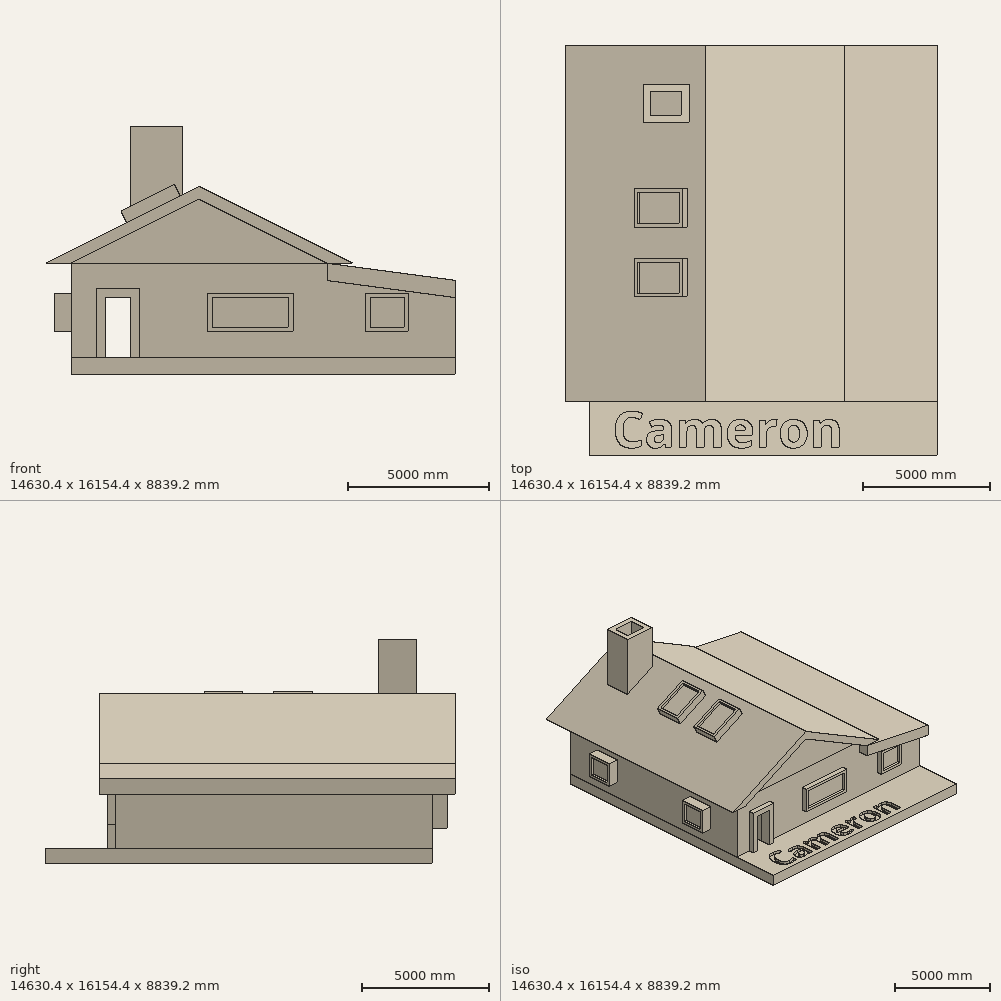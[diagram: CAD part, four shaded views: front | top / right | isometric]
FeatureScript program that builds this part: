
annotation { "Feature Type Name" : "Feature", "Feature Type Description" : "" }
export const myFeature = defineFeature(function(context is Context, id is Id, definition is map)
    precondition{}
    {
        {
            var Q0;
            Q0=qCreatedBy(makeId("Front.planeOp"),FACE);
            var sketch = newSketch(context, id + "F0", { "sketchPlane" : qUnion([Q0])});
            skLineSegment(sketch, "E0", {"start": v(0, 0) * mm, "end": v(-4572, 0) * mm});
            skLineSegment(sketch, "E1", {"start": v(0, 0) * mm, "end": v(4572, 0) * mm});
            skLineSegment(sketch, "E2", {"start": v(0, 0) * mm, "end": v(0, 2286) * mm});
            skLineSegment(sketch, "E3", {"start": v(-4572, 0) * mm, "end": v(0, 2286) * mm});
            skLineSegment(sketch, "E4", {"start": v(0, 2286) * mm, "end": v(4572, 0) * mm});
            skLineSegment(sketch, "E5.bottom", {"start": v(-4572, 0) * mm, "end": v(4572, 0) * mm});
            skLineSegment(sketch, "E5.top", {"start": v(-4572, -3352.8) * mm, "end": v(4572, -3352.8) * mm});
            skLineSegment(sketch, "E5.left", {"start": v(-4572, 0) * mm, "end": v(-4572, -3352.8) * mm});
            skLineSegment(sketch, "E5.right", {"start": v(4572, 0) * mm, "end": v(4572, -3352.8) * mm});
            skLineSegment(sketch, "E6", {"start": v(-4572, 0) * mm, "end": v(-5486.4, 0) * mm});
            skLineSegment(sketch, "E7", {"start": v(4572, 0) * mm, "end": v(5486.4, 0) * mm});
            skLineSegment(sketch, "E8", {"start": v(0, 2286) * mm, "end": v(0, 2743.2) * mm});
            skLineSegment(sketch, "E9", {"start": v(0, 2743.2) * mm, "end": v(-5486.4, 0) * mm});
            skLineSegment(sketch, "E10", {"start": v(0, 2743.2) * mm, "end": v(5486.4, 0) * mm});
            skLineSegment(sketch, "E11", {"start": v(4572, -3352.8) * mm, "end": v(9144, -3352.8) * mm});
            skLineSegment(sketch, "E12", {"start": v(9144, -3352.8) * mm, "end": v(9144, -609.6) * mm});
            skLineSegment(sketch, "E13", {"start": v(9144, -609.6) * mm, "end": v(4572, 0) * mm});
            skLineSegment(sketch, "E14.0", {"start": v(9144, -1224.6) * mm, "end": v(4572, -615) * mm});
            skLineSegment(sketch, "E15.0", {"start": v(4572, -3962.4) * mm, "end": v(9144, -3962.4) * mm});
            skLineSegment(sketch, "E15.1", {"start": v(-4572, -3962.4) * mm, "end": v(4572, -3962.4) * mm});
            skLineSegment(sketch, "E16", {"start": v(-4572, -3962.4) * mm, "end": v(-4572, -3352.8) * mm});
            skLineSegment(sketch, "E17", {"start": v(4572, -3962.4) * mm, "end": v(4572, -3352.8) * mm});
            skLineSegment(sketch, "E18", {"start": v(9144, -3962.4) * mm, "end": v(9144, -3352.8) * mm});
            skLineSegment(sketch, "E19", {"start": v(-3352.8, -3352.8) * mm, "end": v(-2438.4, -3352.8) * mm});
            skLineSegment(sketch, "E20", {"start": v(-2438.4, -3352.8) * mm, "end": v(-2438.4, -1219.2) * mm});
            skLineSegment(sketch, "E21", {"start": v(-2438.4, -1219.2) * mm, "end": v(-3352.8, -1219.2) * mm});
            skLineSegment(sketch, "E22", {"start": v(-3352.8, -1219.2) * mm, "end": v(-3352.8, -3352.8) * mm});
            skLineSegment(sketch, "E23.0", {"start": v(-3657.6, -914.4) * mm, "end": v(-3657.6, -3352.8) * mm});
            skLineSegment(sketch, "E23.1", {"start": v(-2133.6, -914.4) * mm, "end": v(-3657.6, -914.4) * mm});
            skLineSegment(sketch, "E23.2", {"start": v(-2133.6, -3352.8) * mm, "end": v(-2133.6, -914.4) * mm});
            skLineSegment(sketch, "E24", {"start": v(-3657.6, -3352.8) * mm, "end": v(-3352.8, -3352.8) * mm});
            skLineSegment(sketch, "E25", {"start": v(-2438.4, -3352.8) * mm, "end": v(-2133.6, -3352.8) * mm});
            skLineSegment(sketch, "E26", {"start": v(457.2, -2286) * mm, "end": v(3200.4, -2286) * mm});
            skLineSegment(sketch, "E27", {"start": v(457.2, -2286) * mm, "end": v(457.2, -1219.2) * mm});
            skLineSegment(sketch, "E28", {"start": v(457.2, -1219.2) * mm, "end": v(3200.4, -1219.2) * mm});
            skLineSegment(sketch, "E29", {"start": v(3200.4, -1219.2) * mm, "end": v(3200.4, -2286) * mm});
            skLineSegment(sketch, "E30.0", {"start": v(304.8, -2438.4) * mm, "end": v(304.8, -1066.8) * mm});
            skLineSegment(sketch, "E30.1", {"start": v(304.8, -2438.4) * mm, "end": v(3352.8, -2438.4) * mm});
            skLineSegment(sketch, "E30.2", {"start": v(3352.8, -1066.8) * mm, "end": v(3352.8, -2438.4) * mm});
            skLineSegment(sketch, "E30.3", {"start": v(304.8, -1066.8) * mm, "end": v(3352.8, -1066.8) * mm});
            skLineSegment(sketch, "E31", {"start": v(6096, -2286) * mm, "end": v(6096, -1219.2) * mm});
            skLineSegment(sketch, "E32", {"start": v(6096, -2286) * mm, "end": v(7315.2, -2286) * mm});
            skLineSegment(sketch, "E33", {"start": v(7315.2, -2286) * mm, "end": v(7315.2, -1219.2) * mm});
            skLineSegment(sketch, "E34", {"start": v(7315.2, -1219.2) * mm, "end": v(6096, -1219.2) * mm});
            skLineSegment(sketch, "E35.0", {"start": v(7467.6, -1066.8) * mm, "end": v(5943.6, -1066.8) * mm});
            skLineSegment(sketch, "E35.1", {"start": v(7467.6, -2438.4) * mm, "end": v(7467.6, -1066.8) * mm});
            skLineSegment(sketch, "E35.2", {"start": v(5943.6, -2438.4) * mm, "end": v(7467.6, -2438.4) * mm});
            skLineSegment(sketch, "E35.3", {"start": v(5943.6, -2438.4) * mm, "end": v(5943.6, -1066.8) * mm});
            skSolve(sketch);
        }
        {
            var Q0;
            Q0=makeQuery(id+"F0.imprint","IMPRINT",FACE,{"disambiguationData":[TD([[makeQuery(id+"F0.imprint","IMPRINT",EDGE,{"derivedFrom":sQuery(id+"F0.wireOp",EDGE,"E3")}),1.0]])]});
            var Q1;
            Q1=makeQuery(id+"F0.imprint","IMPRINT",FACE,{"disambiguationData":[TD([[makeQuery(id+"F0.imprint","IMPRINT",EDGE,{"derivedFrom":sQuery(id+"F0.wireOp",EDGE,"E4")}),1.0]])]});
            var Q2;
            {var subQ0=sQuery(id+"F0.wireOp",EDGE,"E13");Q2=makeQuery(id+"F0.imprint","IMPRINT",FACE,{"disambiguationData":[TD([[makeQuery(id+"F0.imprint","IMPRINT",EDGE,{"derivedFrom":subQ0}),1.0]])]});}
            extrude(context, id + "F1", {"entities" : qUnion([Q0, Q1, Q2]), "depth" : 914.4 * mm, "offsetDistance" : 30.48 * mm, "hasSecondDirection" : true, "secondDirectionOppositeDirection" : true, "secondDirectionDepth" : 13106.4 * mm});
        }
        {
            var Q0;
            {var subQ0=sQuery(id+"F0.wireOp",EDGE,"E2");Q0=makeQuery(id+"F0.imprint","IMPRINT",FACE,{"disambiguationData":[TD([[makeQuery(id+"F0.imprint","IMPRINT",EDGE,{"derivedFrom":subQ0}),1.0]])]});}
            var Q1;
            {var subQ0=sQuery(id+"F0.wireOp",EDGE,"E2");Q1=makeQuery(id+"F0.imprint","IMPRINT",FACE,{"disambiguationData":[TD([[makeQuery(id+"F0.imprint","IMPRINT",EDGE,{"derivedFrom":subQ0}),-1.0]])]});}
            extrude(context, id + "F2", {"entities" : qUnion([Q0, Q1]), "operationType" : NewBodyOperationType.ADD, "depth" : 304.8 * mm, "offsetDistance" : 30.48 * mm, "hasSecondDirection" : true, "secondDirectionOppositeDirection" : true, "secondDirectionDepth" : 12192 * mm});
        }
        {
            var Q0;
            Q0=makeQuery(id+"F0.imprint","IMPRINT",FACE,{"disambiguationData":[TD([[makeQuery(id+"F0.imprint","IMPRINT",EDGE,{"derivedFrom":sQuery(id+"F0.wireOp",EDGE,"E15.1")}),1.0]])]});
            var Q1;
            Q1=makeQuery(id+"F0.imprint","IMPRINT",FACE,{"disambiguationData":[TD([[makeQuery(id+"F0.imprint","IMPRINT",EDGE,{"derivedFrom":sQuery(id+"F0.wireOp",EDGE,"E11")}),-1.0]])]});
            extrude(context, id + "F3", {"entities" : qUnion([Q0, Q1]), "depth" : 3048 * mm, "offsetDistance" : 30.48 * mm, "hasSecondDirection" : true, "secondDirectionOppositeDirection" : true, "secondDirectionDepth" : 12192 * mm});
        }
        {
            var Q0;
            {var subQ7=sQuery(id+"F0.wireOp",EDGE,"E5.left");Q0=makeQuery(id+"F0.imprint","IMPRINT",FACE,{"disambiguationData":[TD([[makeQuery(id+"F0.imprint","IMPRINT",EDGE,{"derivedFrom":subQ7}),1.0]])]});}
            var Q1;
            Q1=makeQuery(id+"F0.imprint","IMPRINT",FACE,{"disambiguationData":[TD([[makeQuery(id+"F0.imprint","IMPRINT",EDGE,{"derivedFrom":sQuery(id+"F0.wireOp",EDGE,"E20")}),-1.0]])]});
            var Q2;
            Q2=makeQuery(id+"F0.imprint","IMPRINT",FACE,{"disambiguationData":[TD([[makeQuery(id+"F0.imprint","IMPRINT",EDGE,{"derivedFrom":sQuery(id+"F0.wireOp",EDGE,"E19")}),1.0]])]});
            var Q3;
            Q3=makeQuery(id+"F0.imprint","IMPRINT",FACE,{"disambiguationData":[TD([[makeQuery(id+"F0.imprint","IMPRINT",EDGE,{"derivedFrom":sQuery(id+"F0.wireOp",EDGE,"E26")}),1.0]])]});
            var Q4;
            Q4=makeQuery(id+"F0.imprint","IMPRINT",FACE,{"disambiguationData":[TD([[makeQuery(id+"F0.imprint","IMPRINT",EDGE,{"derivedFrom":sQuery(id+"F0.wireOp",EDGE,"E26")}),-1.0]])]});
            var Q5;
            Q5=makeQuery(id+"F0.imprint","IMPRINT",FACE,{"disambiguationData":[TD([[makeQuery(id+"F0.imprint","IMPRINT",EDGE,{"derivedFrom":sQuery(id+"F0.wireOp",EDGE,"E31")}),-1.0]])]});
            var Q6;
            Q6=makeQuery(id+"F0.imprint","IMPRINT",FACE,{"disambiguationData":[TD([[makeQuery(id+"F0.imprint","IMPRINT",EDGE,{"derivedFrom":sQuery(id+"F0.wireOp",EDGE,"E31")}),1.0]])]});
            var Q7;
            {var subQ1=sQuery(id+"F0.wireOp",EDGE,"E11");Q7=makeQuery(id+"F0.imprint","IMPRINT",FACE,{"disambiguationData":[TD([[makeQuery(id+"F0.imprint","IMPRINT",EDGE,{"derivedFrom":subQ1}),1.0]])]});}
            extrude(context, id + "F4", {"entities" : qUnion([Q0, Q1, Q2, Q3, Q4, Q5, Q6, Q7]), "depth" : 304.8 * mm, "offsetDistance" : 30.48 * mm, "hasSecondDirection" : true, "secondDirectionOppositeDirection" : true, "secondDirectionDepth" : 12192 * mm});
        }
        {
            var Q0;
            Q0=makeQuery(id+"F0.imprint","IMPRINT",FACE,{"disambiguationData":[TD([[makeQuery(id+"F0.imprint","IMPRINT",EDGE,{"derivedFrom":sQuery(id+"F0.wireOp",EDGE,"E19")}),1.0]])]});
            var Q1;
            Q1=makeQuery(id+"F0.imprint","IMPRINT",FACE,{"disambiguationData":[TD([[makeQuery(id+"F0.imprint","IMPRINT",EDGE,{"derivedFrom":sQuery(id+"F0.wireOp",EDGE,"E26")}),1.0]])]});
            var Q2;
            Q2=makeQuery(id+"F0.imprint","IMPRINT",FACE,{"disambiguationData":[TD([[makeQuery(id+"F0.imprint","IMPRINT",EDGE,{"derivedFrom":sQuery(id+"F0.wireOp",EDGE,"E31")}),-1.0]])]});
            extrude(context, id + "F5", {"entities" : qUnion([Q0, Q1, Q2]), "depth" : 457.2 * mm, "offsetDistance" : 30.48 * mm});
        }
        {
            var Q0;
            Q0=makeQuery(id+"F0.imprint","IMPRINT",FACE,{"disambiguationData":[TD([[makeQuery(id+"F0.imprint","IMPRINT",EDGE,{"derivedFrom":sQuery(id+"F0.wireOp",EDGE,"E20")}),-1.0]])]});
            var Q1;
            Q1=makeQuery(id+"F0.imprint","IMPRINT",FACE,{"disambiguationData":[TD([[makeQuery(id+"F0.imprint","IMPRINT",EDGE,{"derivedFrom":sQuery(id+"F0.wireOp",EDGE,"E26")}),-1.0]])]});
            var Q2;
            Q2=makeQuery(id+"F0.imprint","IMPRINT",FACE,{"disambiguationData":[TD([[makeQuery(id+"F0.imprint","IMPRINT",EDGE,{"derivedFrom":sQuery(id+"F0.wireOp",EDGE,"E31")}),1.0]])]});
            extrude(context, id + "F6", {"entities" : qUnion([Q0, Q1, Q2]), "depth" : 609.6 * mm, "offsetDistance" : 30.48 * mm});
        }
        {
            var Q0;
            Q0=makeQuery(id+"F4.opExtrude","SWEPT_FACE",FACE,{"disambiguationData":[OSD([sQuery(id+"F0.wireOp",EDGE,"E5.left")])]});
            var sketch = newSketch(context, id + "F7", { "sketchPlane" : qUnion([Q0])});
            skLineSegment(sketch, "E36", {"start": v(-10058.4, -1219.2) * mm, "end": v(-10058.4, -2286) * mm});
            skLineSegment(sketch, "E37", {"start": v(-10058.4, -1219.2) * mm, "end": v(-8839.2, -1219.2) * mm});
            skLineSegment(sketch, "E38", {"start": v(-8839.2, -1219.2) * mm, "end": v(-8839.2, -2286) * mm});
            skLineSegment(sketch, "E39", {"start": v(-8839.2, -2286) * mm, "end": v(-10058.4, -2286) * mm});
            skLineSegment(sketch, "E40", {"start": v(-3048, -1219.2) * mm, "end": v(-3048, -2286) * mm});
            skLineSegment(sketch, "E41", {"start": v(-3048, -2286) * mm, "end": v(-1828.8, -2286) * mm});
            skLineSegment(sketch, "E42", {"start": v(-1828.8, -2286) * mm, "end": v(-1828.8, -1219.2) * mm});
            skLineSegment(sketch, "E43", {"start": v(-1828.8, -1219.2) * mm, "end": v(-3048, -1219.2) * mm});
            skLineSegment(sketch, "E44.0", {"start": v(-10210.8, -1066.8) * mm, "end": v(-8686.8, -1066.8) * mm});
            skLineSegment(sketch, "E44.1", {"start": v(-10210.8, -1066.8) * mm, "end": v(-10210.8, -2438.4) * mm});
            skLineSegment(sketch, "E44.2", {"start": v(-8686.8, -2438.4) * mm, "end": v(-10210.8, -2438.4) * mm});
            skLineSegment(sketch, "E44.3", {"start": v(-8686.8, -1066.8) * mm, "end": v(-8686.8, -2438.4) * mm});
            skLineSegment(sketch, "E45.0", {"start": v(-1676.4, -1066.8) * mm, "end": v(-3200.4, -1066.8) * mm});
            skLineSegment(sketch, "E45.1", {"start": v(-1676.4, -2438.4) * mm, "end": v(-1676.4, -1066.8) * mm});
            skLineSegment(sketch, "E45.2", {"start": v(-3200.4, -2438.4) * mm, "end": v(-1676.4, -2438.4) * mm});
            skLineSegment(sketch, "E45.3", {"start": v(-3200.4, -1066.8) * mm, "end": v(-3200.4, -2438.4) * mm});
            skSolve(sketch);
        }
        {
            var Q0;
            Q0=makeQuery(id+"F7.imprint","IMPRINT",FACE,{"disambiguationData":[TD([[makeQuery(id+"F7.imprint","IMPRINT",EDGE,{"derivedFrom":sQuery(id+"F7.wireOp",EDGE,"E36")}),1.0]])]});
            extrude(context, id + "F8", {"entities" : qUnion([Q0]), "operationType" : NewBodyOperationType.ADD, "depth" : 457.2 * mm, "offsetDistance" : 30.48 * mm});
        }
        {
            var Q0;
            Q0=makeQuery(id+"F1.opExtrude","SWEPT_FACE",FACE,{"disambiguationData":[OSD([sQuery(id+"F0.wireOp",EDGE,"E9")])]});
            var sketch = newSketch(context, id + "F9", { "sketchPlane" : qUnion([Q0])});
            skLineSegment(sketch, "E46", {"start": v(312.4, 6096) * mm, "end": v(312.4, 7315.2) * mm});
            skLineSegment(sketch, "E47", {"start": v(312.4, 7315.2) * mm, "end": v(-1516.4, 7315.2) * mm});
            skLineSegment(sketch, "E48", {"start": v(-1516.4, 6096) * mm, "end": v(312.4, 6096) * mm});
            skLineSegment(sketch, "E49", {"start": v(312.4, 4572) * mm, "end": v(312.4, 3352.8) * mm});
            skLineSegment(sketch, "E50", {"start": v(312.4, 3352.8) * mm, "end": v(-1516.4, 3352.8) * mm});
            skLineSegment(sketch, "E51", {"start": v(-1516.4, 3352.8) * mm, "end": v(-1516.4, 4572) * mm});
            skLineSegment(sketch, "E52", {"start": v(-1516.4, 4572) * mm, "end": v(312.4, 4572) * mm});
            skLineSegment(sketch, "E53", {"start": v(-1516.4, 6096) * mm, "end": v(-1516.4, 7315.2) * mm});
            skLineSegment(sketch, "E54.0", {"start": v(-1668.8, 3200.4) * mm, "end": v(-1668.8, 4724.4) * mm});
            skLineSegment(sketch, "E54.1", {"start": v(464.8, 3200.4) * mm, "end": v(-1668.8, 3200.4) * mm});
            skLineSegment(sketch, "E54.2", {"start": v(464.8, 4724.4) * mm, "end": v(464.8, 3200.4) * mm});
            skLineSegment(sketch, "E54.3", {"start": v(-1668.8, 4724.4) * mm, "end": v(464.8, 4724.4) * mm});
            skLineSegment(sketch, "E55.0", {"start": v(464.8, 5943.6) * mm, "end": v(464.8, 7467.6) * mm});
            skLineSegment(sketch, "E55.1", {"start": v(-1668.8, 5943.6) * mm, "end": v(464.8, 5943.6) * mm});
            skLineSegment(sketch, "E55.2", {"start": v(-1668.8, 5943.6) * mm, "end": v(-1668.8, 7467.6) * mm});
            skLineSegment(sketch, "E55.3", {"start": v(464.8, 7467.6) * mm, "end": v(-1668.8, 7467.6) * mm});
            skSolve(sketch);
        }
        {
            var Q0;
            Q0=makeQuery(id+"F7.imprint","IMPRINT",FACE,{"disambiguationData":[TD([[makeQuery(id+"F7.imprint","IMPRINT",EDGE,{"derivedFrom":sQuery(id+"F7.wireOp",EDGE,"E36")}),-1.0]])]});
            extrude(context, id + "F10", {"entities" : qUnion([Q0]), "operationType" : NewBodyOperationType.ADD, "depth" : 609.6 * mm, "offsetDistance" : 30.48 * mm});
        }
        {
            var Q0;
            Q0 = qSketchRegion(id + "F7", true);
            extrude(context, id + "F11", {"entities" : qUnion([Q0]), "operationType" : NewBodyOperationType.ADD, "depth" : 609.6 * mm, "offsetDistance" : 30.48 * mm});
        }
        {
            var Q0;
            Q0=makeQuery(id+"F11.boolean.opBoolean","SPLIT",FACE,{"disambiguationData":[TD([makeQuery(id+"F11.opExtrude","SWEPT_FACE",FACE,{"disambiguationData":[OSD([sQuery(id+"F7.wireOp",EDGE,"E40")])]})])],"derivedFrom":makeQuery(id+"F4.opExtrude","SWEPT_FACE",FACE,{"disambiguationData":[OSD([sQuery(id+"F0.wireOp",EDGE,"E5.left")])]})});
            extrude(context, id + "F12", {"entities" : qUnion([Q0]), "operationType" : NewBodyOperationType.ADD, "depth" : 457.2 * mm, "offsetDistance" : 30.48 * mm});
        }
        {
            var Q0;
            Q0=makeQuery(id+"F3.opExtrude","SWEPT_FACE",FACE,{"disambiguationData":[OSD([sQuery(id+"F0.wireOp",EDGE,"E15.0"),sQuery(id+"F0.wireOp",EDGE,"E15.1")])]});
            var sketch = newSketch(context, id + "F13", { "sketchPlane" : qUnion([Q0])});
            skLineSegment(sketch, "E56", {"start": v(-2133.6, -10363.2) * mm, "end": v(-914.4, -10363.2) * mm});
            skLineSegment(sketch, "E57", {"start": v(-914.4, -10363.2) * mm, "end": v(-914.4, -11277.6) * mm});
            skLineSegment(sketch, "E58", {"start": v(-914.4, -11277.6) * mm, "end": v(-2133.6, -11277.6) * mm});
            skLineSegment(sketch, "E59", {"start": v(-2133.6, -11277.6) * mm, "end": v(-2133.6, -10363.2) * mm});
            skLineSegment(sketch, "E60.0", {"start": v(-2438.4, -10058.4) * mm, "end": v(-609.6, -10058.4) * mm});
            skLineSegment(sketch, "E60.1", {"start": v(-2438.4, -11582.4) * mm, "end": v(-2438.4, -10058.4) * mm});
            skLineSegment(sketch, "E60.2", {"start": v(-609.6, -11582.4) * mm, "end": v(-2438.4, -11582.4) * mm});
            skLineSegment(sketch, "E60.3", {"start": v(-609.6, -10058.4) * mm, "end": v(-609.6, -11582.4) * mm});
            skSolve(sketch);
        }
        {
            var Q0;
            Q0=makeQuery(id+"F13.imprint","IMPRINT",FACE,{"disambiguationData":[TD([[makeQuery(id+"F13.imprint","IMPRINT",EDGE,{"derivedFrom":sQuery(id+"F13.wireOp",EDGE,"E56")}),1.0]])]});
            extrude(context, id + "F14", {"entities" : qUnion([Q0]), "oppositeDirection" : true, "depth" : 8839.2 * mm, "offsetDistance" : 30.48 * mm});
        }
        {
            var Q0;
            Q0=makeQuery(id+"F9.imprint","IMPRINT",FACE,{"disambiguationData":[TD([[makeQuery(id+"F9.imprint","IMPRINT",EDGE,{"derivedFrom":sQuery(id+"F9.wireOp",EDGE,"E46")}),-1.0]])]});
            var Q1;
            Q1=makeQuery(id+"F9.imprint","IMPRINT",FACE,{"disambiguationData":[TD([[makeQuery(id+"F9.imprint","IMPRINT",EDGE,{"derivedFrom":sQuery(id+"F9.wireOp",EDGE,"E49")}),1.0]])]});
            extrude(context, id + "F15", {"entities" : qUnion([Q0, Q1]), "operationType" : NewBodyOperationType.ADD, "depth" : 457.2 * mm, "offsetDistance" : 30.48 * mm});
        }
        {
            var Q0;
            Q0=makeQuery(id+"F15.boolean.opBoolean","SPLIT",FACE,{"disambiguationData":[TD([makeQuery(id+"F15.opExtrude","SWEPT_FACE",FACE,{"disambiguationData":[OSD([sQuery(id+"F9.wireOp",EDGE,"E46")])]})])],"derivedFrom":makeQuery(id+"F1.opExtrude","SWEPT_FACE",FACE,{"disambiguationData":[OSD([sQuery(id+"F0.wireOp",EDGE,"E9")])]})});
            var Q1;
            Q1=makeQuery(id+"F15.boolean.opBoolean","SPLIT",FACE,{"disambiguationData":[TD([makeQuery(id+"F15.opExtrude","SWEPT_FACE",FACE,{"disambiguationData":[OSD([sQuery(id+"F9.wireOp",EDGE,"E49")])]})])],"derivedFrom":makeQuery(id+"F1.opExtrude","SWEPT_FACE",FACE,{"disambiguationData":[OSD([sQuery(id+"F0.wireOp",EDGE,"E9")])]})});
            extrude(context, id + "F16", {"entities" : qUnion([Q0, Q1]), "operationType" : NewBodyOperationType.ADD, "depth" : 304.8 * mm, "offsetDistance" : 30.48 * mm});
        }
        {
            var Q0;
            Q0=makeQuery(id+"F4.opExtrude","CAP_FACE",FACE,{"disambiguationData":[OSD([sQuery(id+"F0.wireOp",EDGE,"E5.bottom"),sQuery(id+"F0.wireOp",EDGE,"E5.top"),sQuery(id+"F0.wireOp",EDGE,"E5.left"),sQuery(id+"F0.wireOp",EDGE,"E5.right"),sQuery(id+"F0.wireOp",EDGE,"E11"),sQuery(id+"F0.wireOp",EDGE,"E12"),sQuery(id+"F0.wireOp",EDGE,"E14.0"),sQuery(id+"F0.wireOp",EDGE,"E19"),sQuery(id+"F0.wireOp",EDGE,"E24"),sQuery(id+"F0.wireOp",EDGE,"E25")])],"isStart":true});
            var sketch = newSketch(context, id + "F17", { "sketchPlane" : qUnion([Q0])});
            skLineSegment(sketch, "E61.bottom", {"start": v(-4358.64, -1219.2) * mm, "end": v(-1920.24, -1219.2) * mm});
            skLineSegment(sketch, "E61.top", {"start": v(-4358.64, -2438.4) * mm, "end": v(-1920.24, -2438.4) * mm});
            skLineSegment(sketch, "E61.left", {"start": v(-4358.64, -1219.2) * mm, "end": v(-4358.64, -2438.4) * mm});
            skLineSegment(sketch, "E61.right", {"start": v(-1920.24, -1219.2) * mm, "end": v(-1920.24, -2438.4) * mm});
            skLineSegment(sketch, "E62.0", {"start": v(-4511.04, -1066.8) * mm, "end": v(-1767.84, -1066.8) * mm});
            skLineSegment(sketch, "E62.1", {"start": v(-4511.04, -1066.8) * mm, "end": v(-4511.04, -2590.8) * mm});
            skLineSegment(sketch, "E62.2", {"start": v(-4511.04, -2590.8) * mm, "end": v(-1767.84, -2590.8) * mm});
            skLineSegment(sketch, "E62.3", {"start": v(-1767.84, -1066.8) * mm, "end": v(-1767.84, -2590.8) * mm});
            skSolve(sketch);
        }
        {
            var Q0;
            Q0=makeQuery(id+"F17.imprint","IMPRINT",FACE,{"disambiguationData":[TD([[makeQuery(id+"F17.imprint","IMPRINT",EDGE,{"derivedFrom":sQuery(id+"F17.wireOp",EDGE,"E61.bottom")}),1.0]])]});
            extrude(context, id + "F18", {"entities" : qUnion([Q0]), "operationType" : NewBodyOperationType.ADD, "depth" : 609.6 * mm, "offsetDistance" : 30.48 * mm, "hasSecondDirection" : true, "secondDirectionOppositeDirection" : true, "secondDirectionDepth" : 609.6 * mm});
        }
        {
            var Q0;
            Q0=makeQuery(id+"F18.boolean.opBoolean","SPLIT",FACE,{"disambiguationData":[TD([makeQuery(id+"F18.opExtrude","SWEPT_FACE",FACE,{"disambiguationData":[OSD([sQuery(id+"F17.wireOp",EDGE,"E61.bottom")])]})])],"derivedFrom":makeQuery(id+"F4.opExtrude","CAP_FACE",FACE,{"disambiguationData":[OSD([sQuery(id+"F0.wireOp",EDGE,"E5.bottom"),sQuery(id+"F0.wireOp",EDGE,"E5.top"),sQuery(id+"F0.wireOp",EDGE,"E5.left"),sQuery(id+"F0.wireOp",EDGE,"E5.right"),sQuery(id+"F0.wireOp",EDGE,"E11"),sQuery(id+"F0.wireOp",EDGE,"E12"),sQuery(id+"F0.wireOp",EDGE,"E14.0"),sQuery(id+"F0.wireOp",EDGE,"E19"),sQuery(id+"F0.wireOp",EDGE,"E24"),sQuery(id+"F0.wireOp",EDGE,"E25")])],"isStart":true})});
            extrude(context, id + "F19", {"entities" : qUnion([Q0]), "operationType" : NewBodyOperationType.ADD, "depth" : 457.2 * mm, "offsetDistance" : 30.48 * mm, "hasSecondDirection" : true, "secondDirectionOppositeDirection" : true, "secondDirectionDepth" : 457.2 * mm});
        }
        {
            var Q0;
            Q0=makeQuery(id+"F3.opExtrude","SWEPT_FACE",FACE,{"disambiguationData":[OSD([sQuery(id+"F0.wireOp",EDGE,"E5.top"),sQuery(id+"F0.wireOp",EDGE,"E11"),sQuery(id+"F0.wireOp",EDGE,"E19"),sQuery(id+"F0.wireOp",EDGE,"E24"),sQuery(id+"F0.wireOp",EDGE,"E25")])]});
            var sketch = newSketch(context, id + "F20", { "sketchPlane" : qUnion([Q0])});
            skText(sketch, "E63", { "text": "Cameron", "fontName": "OpenSans-Bold.ttf"});
            const initialGuessF20  = {"E63": [-3.6576, -2.7432, 1, 0, 1.4401]};
            skSetInitialGuess(sketch, initialGuessF20);
            skSolve(sketch);
        }
        {
            var Q0;
            Q0=makeQuery(id+"F20.imprint","IMPRINT",FACE,{"disambiguationData":[TD([[makeQuery(id+"F20.imprint","IMPRINT",EDGE,{"derivedFrom":sQuery(id+"F20.wireOp",EDGE,"E63.sketch_text.stroke-0")}),-1.0]])]});
            var Q1;
            Q1=makeQuery(id+"F20.imprint","IMPRINT",FACE,{"disambiguationData":[TD([[makeQuery(id+"F20.imprint","IMPRINT",EDGE,{"derivedFrom":sQuery(id+"F20.wireOp",EDGE,"E63.sketch_text.stroke-15")}),-1.0]])]});
            var Q2;
            Q2=makeQuery(id+"F20.imprint","IMPRINT",FACE,{"disambiguationData":[TD([[makeQuery(id+"F20.imprint","IMPRINT",EDGE,{"derivedFrom":sQuery(id+"F20.wireOp",EDGE,"E63.sketch_text.stroke-40")}),-1.0]])]});
            var Q3;
            Q3=makeQuery(id+"F20.imprint","IMPRINT",FACE,{"disambiguationData":[TD([[makeQuery(id+"F20.imprint","IMPRINT",EDGE,{"derivedFrom":sQuery(id+"F20.wireOp",EDGE,"E63.sketch_text.stroke-68")}),-1.0]])]});
            var Q4;
            Q4=makeQuery(id+"F20.imprint","IMPRINT",FACE,{"disambiguationData":[TD([[makeQuery(id+"F20.imprint","IMPRINT",EDGE,{"derivedFrom":sQuery(id+"F20.wireOp",EDGE,"E63.sketch_text.stroke-88")}),-1.0]])]});
            var Q5;
            Q5=makeQuery(id+"F20.imprint","IMPRINT",FACE,{"disambiguationData":[TD([[makeQuery(id+"F20.imprint","IMPRINT",EDGE,{"derivedFrom":sQuery(id+"F20.wireOp",EDGE,"E63.sketch_text.stroke-101")}),-1.0]])]});
            var Q6;
            Q6=makeQuery(id+"F20.imprint","IMPRINT",FACE,{"disambiguationData":[TD([[makeQuery(id+"F20.imprint","IMPRINT",EDGE,{"derivedFrom":sQuery(id+"F20.wireOp",EDGE,"E63.sketch_text.stroke-119")}),-1.0]])]});
            extrude(context, id + "F21", {"entities" : qUnion([Q0, Q1, Q2, Q3, Q4, Q5, Q6]), "operationType" : NewBodyOperationType.REMOVE, "oppositeDirection" : true, "depth" : 152.4 * mm, "offsetDistance" : 30.48 * mm});
        }
    });
